# Revit family: 306_6629b1c502e64965be3f615117b54c
name_source: partatom
category: Pipe Accessories
units: mm (PartAtom-declared; Revit-internal decimal feet)

## family parameters
Always vertical = Yes
Cut with Voids When Loaded = No
Part Type = Valve - Breaks Into
Round Connector Dimension = Use Diameter
Shared = No
Work Plane-Based = No

## types (3) — shared parameters
Description = Chrome-pl.thermostatic mixer, setting range 25÷65°C, F conn.
H2 = 35 mm  [stored 0.114829 ft]
H2HH = 28 mm  [stored 0.0918635 ft]
H2HH__ve = -28 mm
HH = 15 mm  [stored 0.0492126 ft]
HH2 = 8 mm  [stored 0.0262467 ft]
L22 = 2 mm  [stored 0.00656168 ft]
L2D = 74 mm
L2D_Min = 3048 mm  [stored 10 ft]
L5 = 5 mm  [stored 0.0164042 ft]
LH = 23 mm
LL = 3 mm  [stored 0.00984252 ft]
LL__ve = -3 mm  [stored -0.00984252 ft]
Manufacturer = FAR
QmdConnectorList = 301;D;302;D
SW = No
W2D = 25 mm  [stored 0.082021 ft]
magiPartTypeId = 306
magiProductFamilyId = 6629b1c502e64965be3f615117b54c

## per-type parameters (varying)
| type | B | BNTL | CenSd_R3_6 | D | L2 | LNT | LNT__ve | NT | NT__ve | R | R1 | R11 | R2 | R3 | magiProductId |
| 3950 1 | 42 mm  [stored 0.137795 ft] | 19 mm | 16 mm | 25 mm | 37 mm | 43 mm | -43 mm | 12 mm  [stored 0.0393701 ft] | -12 mm | 13 mm | 17 mm | 18 mm | 15 mm  [stored 0.0492126 ft] | 19 mm | a1d091abba0f428f9d4d36eb20d7b7 |
| 3950 12 | 38 mm | 17 mm | 12 mm  [stored 0.0393701 ft] | 15 mm | 33 mm | 38 mm | -38 mm | 11 mm  [stored 0.0360892 ft] | -11 mm | 8 mm  [stored 0.0262467 ft] | 12 mm  [stored 0.0393701 ft] | 13 mm | 10 mm  [stored 0.0328084 ft] | 14 mm  [stored 0.0459318 ft] | 1112938704284558bcf35aaa71b303 |
| 3950 34 | 39 mm | 17 mm | 14 mm  [stored 0.0459318 ft] | 20 mm | 35 mm  [stored 0.114829 ft] | 41 mm | -41 mm | 12 mm  [stored 0.0393701 ft] | -12 mm | 10 mm  [stored 0.0328084 ft] | 14 mm  [stored 0.0459318 ft] | 15 mm  [stored 0.0492126 ft] | 13 mm | 16 mm | 21faba62c55c4e6aac4e789e232d6e |

note: column(s) folded — value = type name in every type: MC Product Code

note: [stored X ft] marks values corroborated as IEEE doubles in the binary element streams (Revit-internal decimal feet)

## geometry (parser evidence)
native form markers: Sweep x3
no freeform markers — native parametric forms only
